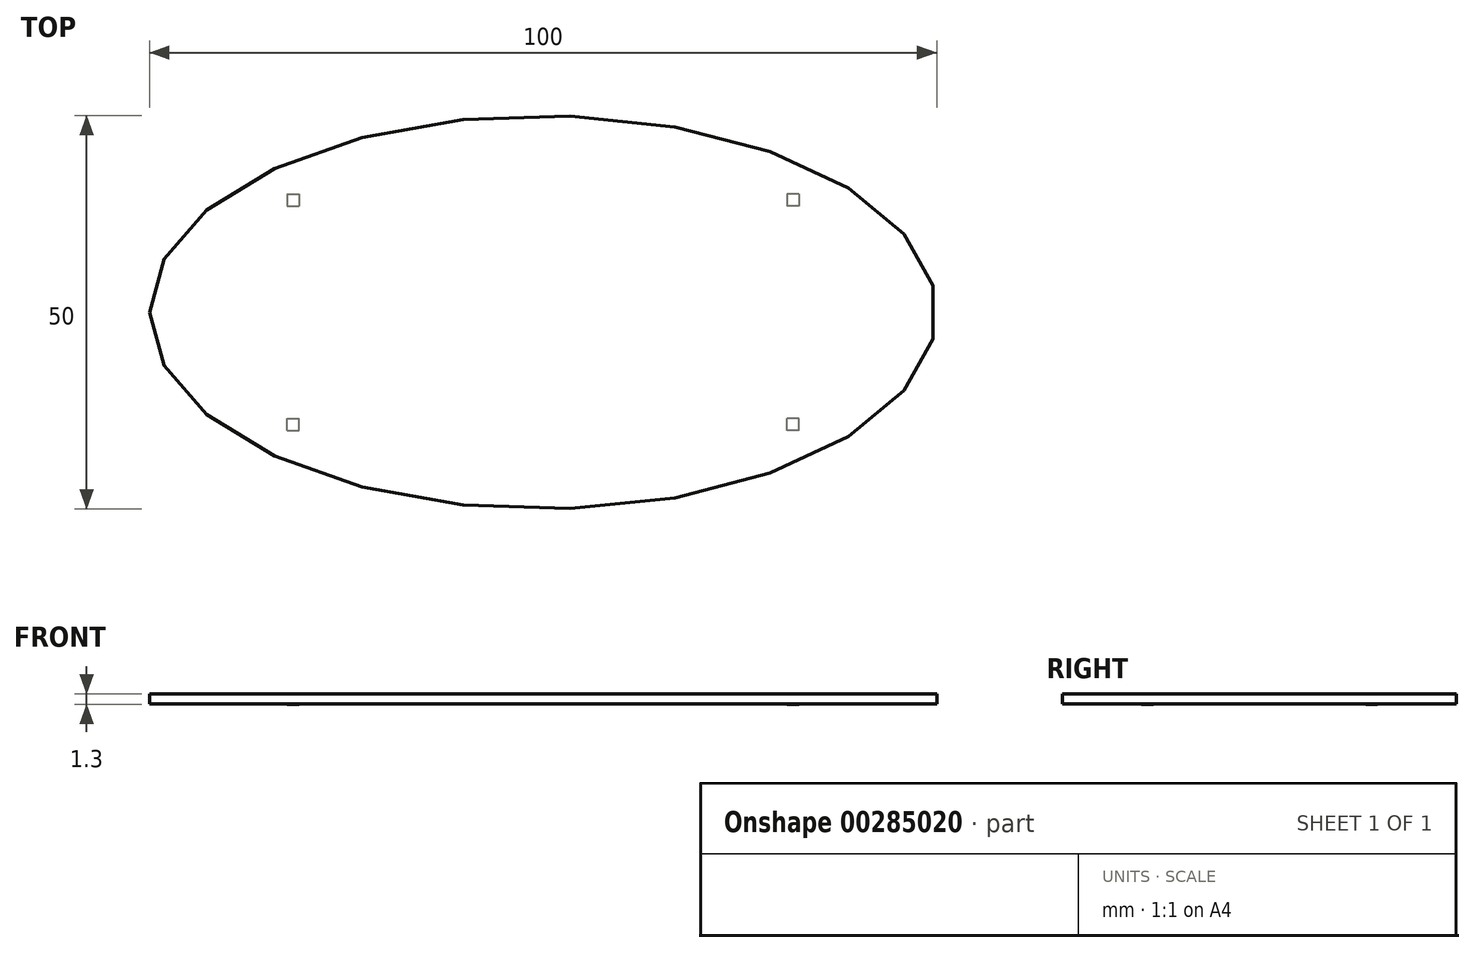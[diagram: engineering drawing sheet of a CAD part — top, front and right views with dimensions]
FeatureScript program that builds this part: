
annotation { "Feature Type Name" : "Feature", "Feature Type Description" : "" }
export const myFeature = defineFeature(function(context is Context, id is Id, definition is map)
    precondition{}
    {
        {
            var Q0;
            Q0=qCreatedBy(makeId("Top.planeOp"),FACE);
            var sketch = newSketch(context, id + "F0", { "sketchPlane" : qUnion([Q0])});
            skEllipse(sketch, "E0", {"center": v(0, 0) * mm, "majorRadius": 1000 * mm, "minorRadius": 500 * mm, "majorAxis": v(-1, 0)});
            skSolve(sketch);
        }
        {
            var Q0;
            Q0 = qSketchRegion(id + "F0", true);
            extrude(context, id + "F1", {"entities" : qUnion([Q0]), "depth" : 25 * mm});
        }
        {
            var Q0;
            Q0=makeQuery(id+"F1.opExtrude","CAP_FACE",FACE,{"disambiguationData":[OSD([sQuery(id+"F0.wireOp",EDGE,"E0")])],"isStart":true});
            var sketch = newSketch(context, id + "F2", { "sketchPlane" : qUnion([Q0])});
            skLineSegment(sketch, "E1", {"start": v(-1000, 0) * mm, "end": v(1000, 0) * mm, "construction": true});
            skLineSegment(sketch, "E2", {"start": v(0, 500) * mm, "end": v(0, -500) * mm, "construction": true});
            skLineSegment(sketch, "E3", {"start": v(-650, 0) * mm, "end": v(-650, 300) * mm, "construction": true});
            skLineSegment(sketch, "E4", {"start": v(-650, 300) * mm, "end": v(0, 300) * mm, "construction": true});
            skLineSegment(sketch, "E5.bottom", {"start": v(-650, 300) * mm, "end": v(-620, 300) * mm});
            skLineSegment(sketch, "E5.top", {"start": v(-650, 270) * mm, "end": v(-620, 270) * mm});
            skLineSegment(sketch, "E5.left", {"start": v(-650, 300) * mm, "end": v(-650, 270) * mm});
            skLineSegment(sketch, "E5.right", {"start": v(-620, 300) * mm, "end": v(-620, 270) * mm});
            skLineSegment(sketch, "E6", {"start": v(-650, 0) * mm, "end": v(-650, -300) * mm, "construction": true});
            skLineSegment(sketch, "E7", {"start": v(-650, -300) * mm, "end": v(0, -300) * mm, "construction": true});
            skLineSegment(sketch, "E8.bottom", {"start": v(-650, -300) * mm, "end": v(-620, -300) * mm});
            skLineSegment(sketch, "E8.top", {"start": v(-650, -270) * mm, "end": v(-620, -270) * mm});
            skLineSegment(sketch, "E8.left", {"start": v(-650, -300) * mm, "end": v(-650, -270) * mm});
            skLineSegment(sketch, "E8.right", {"start": v(-620, -300) * mm, "end": v(-620, -270) * mm});
            skLineSegment(sketch, "E9.bottom", {"start": v(0, 300) * mm, "end": v(650, 300) * mm, "construction": true});
            skLineSegment(sketch, "E9.top", {"start": v(0, 0) * mm, "end": v(650, 0) * mm, "construction": true});
            skLineSegment(sketch, "E9.left", {"start": v(0, 300) * mm, "end": v(0, 0) * mm, "construction": true});
            skLineSegment(sketch, "E9.right", {"start": v(650, 300) * mm, "end": v(650, 0) * mm, "construction": true});
            skLineSegment(sketch, "E10.top", {"start": v(0, -300) * mm, "end": v(650, -300) * mm, "construction": true});
            skLineSegment(sketch, "E10.left", {"start": v(0, 0) * mm, "end": v(0, -300) * mm, "construction": true});
            skLineSegment(sketch, "E10.right", {"start": v(650, 0) * mm, "end": v(650, -300) * mm, "construction": true});
            skLineSegment(sketch, "E11.bottom", {"start": v(650, 300) * mm, "end": v(620, 300) * mm});
            skLineSegment(sketch, "E11.top", {"start": v(650, 270) * mm, "end": v(620, 270) * mm});
            skLineSegment(sketch, "E11.left", {"start": v(650, 300) * mm, "end": v(650, 270) * mm});
            skLineSegment(sketch, "E11.right", {"start": v(620, 300) * mm, "end": v(620, 270) * mm});
            skLineSegment(sketch, "E12.bottom", {"start": v(650, -300) * mm, "end": v(620, -300) * mm});
            skLineSegment(sketch, "E12.top", {"start": v(650, -270) * mm, "end": v(620, -270) * mm});
            skLineSegment(sketch, "E12.left", {"start": v(650, -300) * mm, "end": v(650, -270) * mm});
            skLineSegment(sketch, "E12.right", {"start": v(620, -300) * mm, "end": v(620, -270) * mm});
            skSolve(sketch);
        }
        {
            var Q0;
            Q0=makeQuery(id+"F2.imprint","IMPRINT",FACE,{"disambiguationData":[TD([[makeQuery(id+"F2.imprint","IMPRINT",EDGE,{"derivedFrom":sQuery(id+"F2.wireOp",EDGE,"E11.bottom")}),1.0]])]});
            var Q1;
            Q1=makeQuery(id+"F2.imprint","IMPRINT",FACE,{"disambiguationData":[TD([[makeQuery(id+"F2.imprint","IMPRINT",EDGE,{"derivedFrom":sQuery(id+"F2.wireOp",EDGE,"E12.bottom")}),-1.0]])]});
            var Q2;
            Q2=makeQuery(id+"F2.imprint","IMPRINT",FACE,{"disambiguationData":[TD([[makeQuery(id+"F2.imprint","IMPRINT",EDGE,{"derivedFrom":sQuery(id+"F2.wireOp",EDGE,"E8.bottom")}),1.0]])]});
            var Q3;
            Q3=makeQuery(id+"F2.imprint","IMPRINT",FACE,{"disambiguationData":[TD([[makeQuery(id+"F2.imprint","IMPRINT",EDGE,{"derivedFrom":sQuery(id+"F2.wireOp",EDGE,"E5.bottom")}),-1.0]])]});
            extrude(context, id + "F3", {"entities" : qUnion([Q0, Q1, Q2, Q3]), "operationType" : NewBodyOperationType.ADD, "depth" : 1 * mm});
        }
        {
            var Q0;
            Q0=makeQuery(id+"F1.opExtrude","SWEPT_BODY",BODY,{"disambiguationData":[OSD([sQuery(id+"F0.wireOp",EDGE,"E0")])]});
            var Q1;
            Q1=qCreatedBy(makeId("Origin.pointOp"),VERTEX);
            transform(context, id + "F4", {"entities" : qUnion([Q0]), "transformType" : TransformType.SCALE_UNIFORMLY, "scale" : 0.05, "scalePoint" : qUnion([Q1]), "makeCopy" : false});
        }
    });
